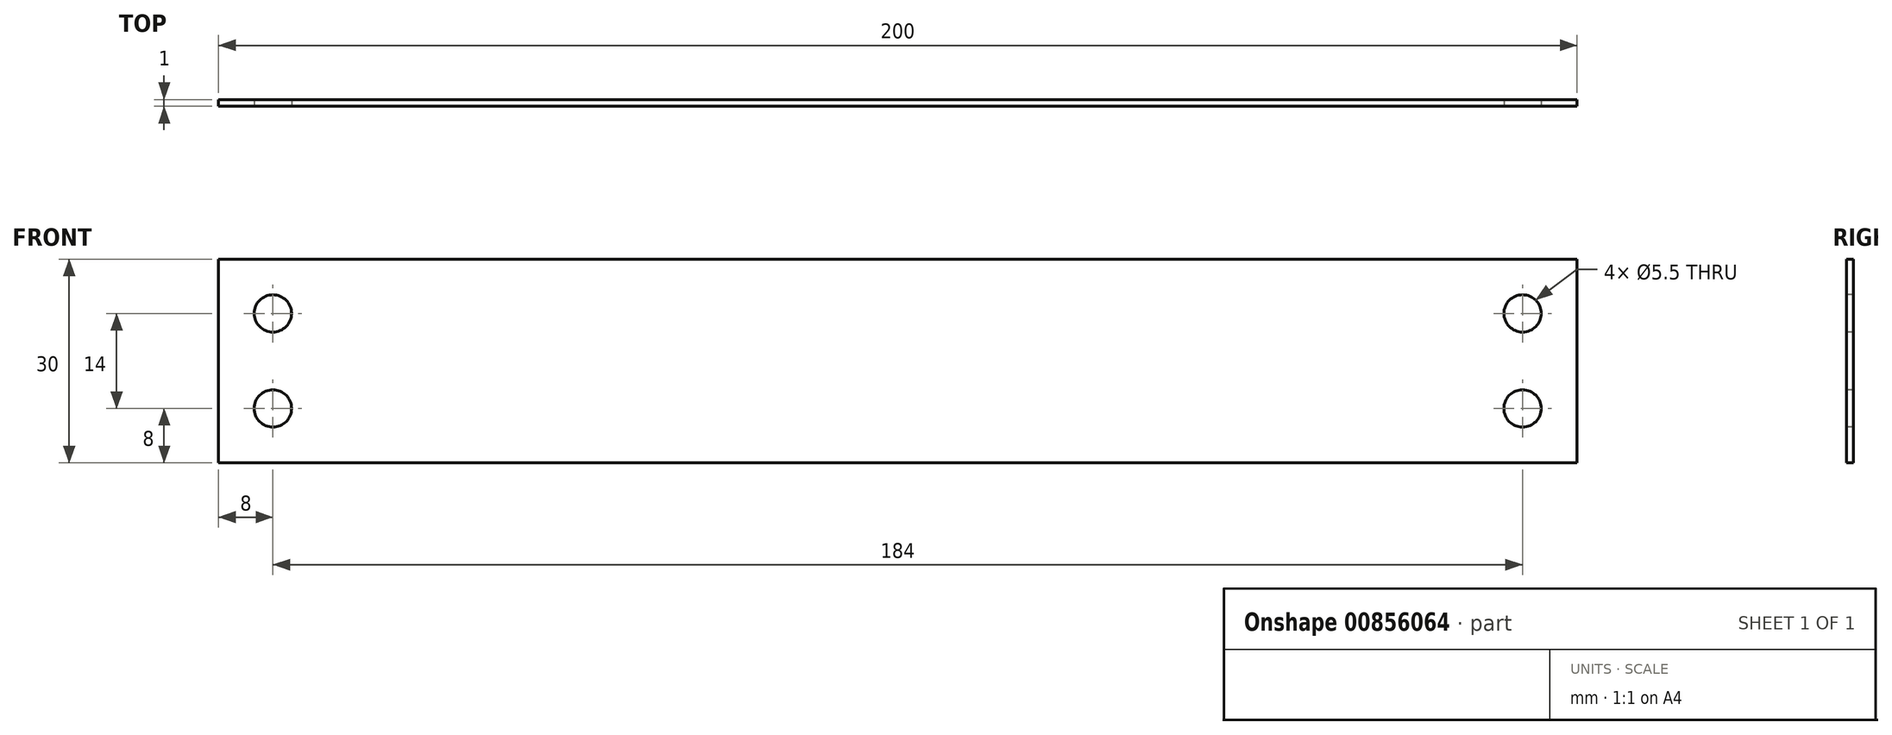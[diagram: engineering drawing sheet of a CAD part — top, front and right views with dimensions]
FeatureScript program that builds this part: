
annotation { "Feature Type Name" : "Feature", "Feature Type Description" : "" }
export const myFeature = defineFeature(function(context is Context, id is Id, definition is map)
    precondition{}
    {
        {
            var Q0;
            Q0=qCreatedBy(makeId("Front.planeOp"),FACE);
            var sketch = newSketch(context, id + "F0", { "sketchPlane" : qUnion([Q0])});
            skLineSegment(sketch, "E0.bottom", {"start": v(100, 15) * mm, "end": v(-100, 15) * mm});
            skLineSegment(sketch, "E0.top", {"start": v(100, -15) * mm, "end": v(-100, -15) * mm});
            skLineSegment(sketch, "E0.left", {"start": v(100, 15) * mm, "end": v(100, -15) * mm});
            skLineSegment(sketch, "E0.right", {"start": v(-100, 15) * mm, "end": v(-100, -15) * mm});
            skPoint(sketch, "E0.middle", {"position": v(0, 0) * mm});
            skSolve(sketch);
        }
        {
            var Q0;
            Q0=makeQuery(id+"F0.imprint","IMPRINT",FACE,{"disambiguationData":[TD([[makeQuery(id+"F0.imprint","IMPRINT",EDGE,{"derivedFrom":sQuery(id+"F0.wireOp",EDGE,"E0.bottom")}),1.0]])]});
            extrude(context, id + "F1", {"entities" : qUnion([Q0]), "depth" : 1 * mm, "offsetDistance" : 25 * mm});
        }
        {
            var Q0;
            Q0=makeQuery(id+"F1.opExtrude","CAP_FACE",FACE,{"disambiguationData":[OSD([sQuery(id+"F0.wireOp",EDGE,"E0.bottom"),sQuery(id+"F0.wireOp",EDGE,"E0.top"),sQuery(id+"F0.wireOp",EDGE,"E0.left"),sQuery(id+"F0.wireOp",EDGE,"E0.right")])],"isStart":false});
            var sketch = newSketch(context, id + "F2", { "sketchPlane" : qUnion([Q0])});
            skLineSegment(sketch, "E1", {"start": v(-100, 15) * mm, "end": v(-92, 15) * mm});
            skLineSegment(sketch, "E2", {"start": v(-92, 15) * mm, "end": v(-92, 7) * mm});
            skLineSegment(sketch, "E3", {"start": v(-100, -15) * mm, "end": v(-92, -15) * mm});
            skLineSegment(sketch, "E4", {"start": v(-92, -15) * mm, "end": v(-92, -7) * mm});
            skLineSegment(sketch, "E5", {"start": v(100, 15) * mm, "end": v(92, 15) * mm});
            skLineSegment(sketch, "E6", {"start": v(92, 15) * mm, "end": v(92, 7) * mm});
            skLineSegment(sketch, "E7", {"start": v(100, -15) * mm, "end": v(92, -15) * mm});
            skLineSegment(sketch, "E8", {"start": v(92, -15) * mm, "end": v(92, -7) * mm});
            skSolve(sketch);
        }
        {
            var Q0;
            Q0=sQuery(id+"F2.wireOp",VERTEX,"E4.end");
            var Q1;
            Q1=sQuery(id+"F2.wireOp",VERTEX,"E2.end");
            var Q2;
            Q2=sQuery(id+"F2.wireOp",VERTEX,"E6.end");
            var Q3;
            Q3=sQuery(id+"F2.wireOp",VERTEX,"E8.end");
            var Q4;
            Q4=makeQuery(id+"F1.opExtrude","SWEPT_BODY",BODY,{"disambiguationData":[OSD([sQuery(id+"F0.wireOp",EDGE,"E0.bottom"),sQuery(id+"F0.wireOp",EDGE,"E0.top"),sQuery(id+"F0.wireOp",EDGE,"E0.left"),sQuery(id+"F0.wireOp",EDGE,"E0.right")])]});
            hole(context, id + "F3", {"style" : HoleStyle.SIMPLE, "endStyle" : HoleEndStyle.THROUGH, "standardTappedOrClearance" : lookupTablePath({ "fit" : "Normal", "standard" : "ISO", "size" : "M5", "type" : "Clearance" }), "standardBlindInLast" : lookupTablePath({ "fit" : "Standard", "standard" : "ISO", "size" : "M5", "type" : "Clearance" }), "holeDiameter" : 5.5 * mm, "majorDiameter" : 5 * mm, "isTappedThrough" : true, "tappedDepth" : 12 * mm, "tapClearance" : 3, "locations" : qUnion([Q0, Q1, Q2, Q3]), "scope" : qUnion([Q4])});
        }
    });
